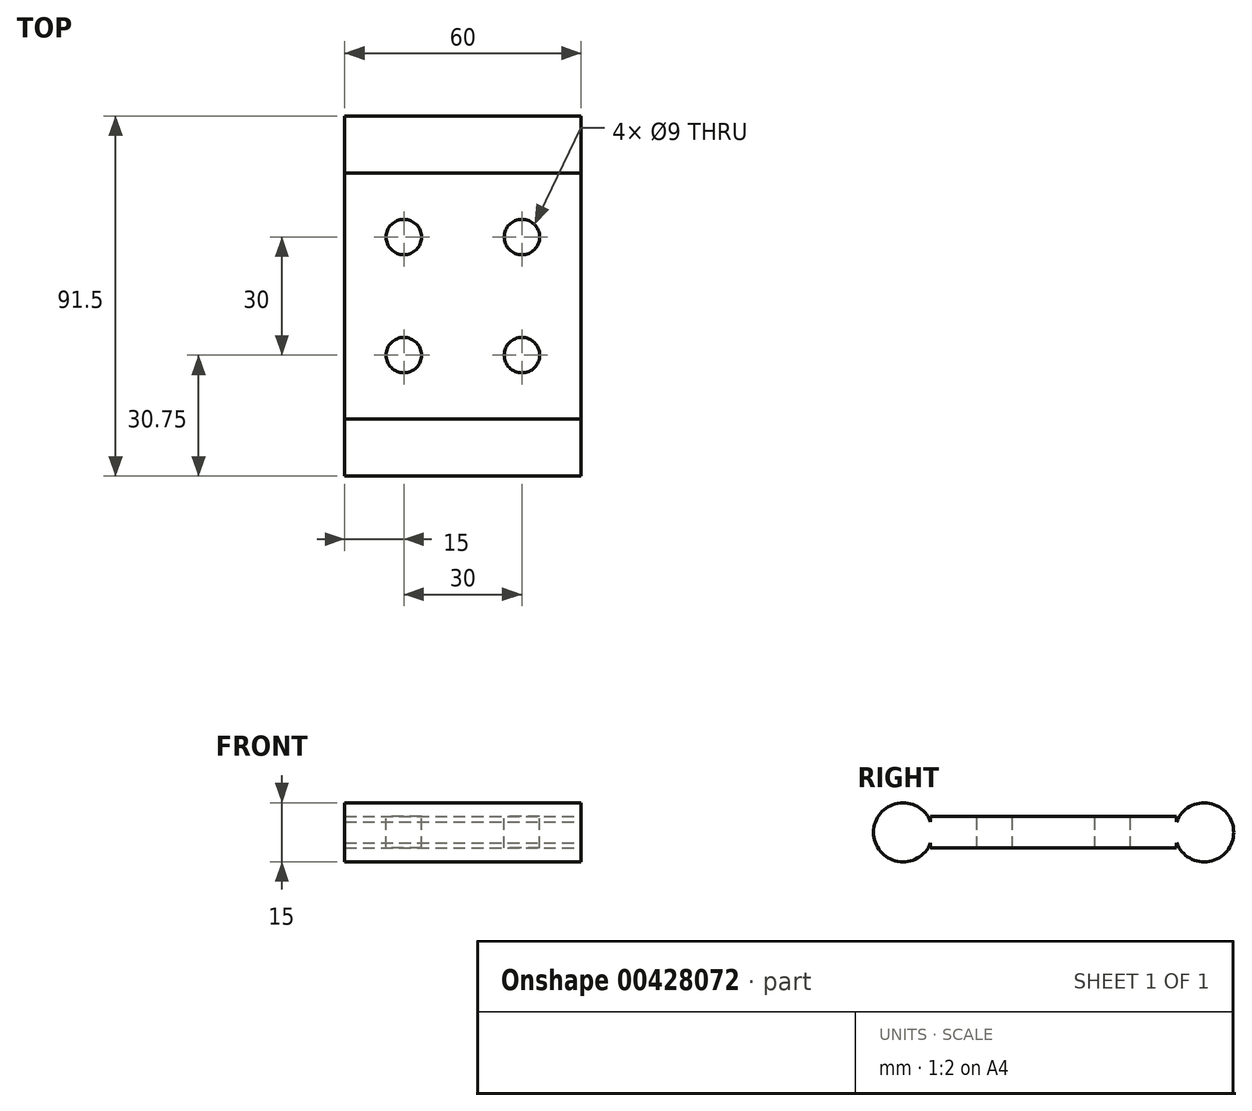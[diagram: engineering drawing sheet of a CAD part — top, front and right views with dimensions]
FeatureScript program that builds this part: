
annotation { "Feature Type Name" : "Feature", "Feature Type Description" : "" }
export const myFeature = defineFeature(function(context is Context, id is Id, definition is map)
    precondition{}
    {
        {
            var Q0;
            Q0=qCreatedBy(makeId("Top.planeOp"),FACE);
            var sketch = newSketch(context, id + "F0", { "sketchPlane" : qUnion([Q0])});
            skLineSegment(sketch, "E0.bottom", {"start": v(0, 0) * mm, "end": v(60, 0) * mm});
            skLineSegment(sketch, "E0.top", {"start": v(0, -62.5) * mm, "end": v(60, -62.5) * mm});
            skLineSegment(sketch, "E0.left", {"start": v(0, 0) * mm, "end": v(0, -62.5) * mm});
            skLineSegment(sketch, "E0.right", {"start": v(60, 0) * mm, "end": v(60, -62.5) * mm});
            skSolve(sketch);
        }
        {
            var Q0;
            Q0=makeQuery(id+"F0.imprint","IMPRINT",FACE,{"disambiguationData":[TD([[makeQuery(id+"F0.imprint","IMPRINT",EDGE,{"derivedFrom":sQuery(id+"F0.wireOp",EDGE,"E0.bottom")}),-1.0]])]});
            extrude(context, id + "F1", {"entities" : qUnion([Q0]), "depth" : 8 * mm});
        }
        {
            var Q0;
            Q0=makeQuery(id+"F1.opExtrude","CAP_FACE",FACE,{"disambiguationData":[OSD([sQuery(id+"F0.wireOp",EDGE,"E0.bottom"),sQuery(id+"F0.wireOp",EDGE,"E0.top"),sQuery(id+"F0.wireOp",EDGE,"E0.left"),sQuery(id+"F0.wireOp",EDGE,"E0.right")])],"isStart":false});
            var sketch = newSketch(context, id + "F2", { "sketchPlane" : qUnion([Q0])});
            skLineSegment(sketch, "E1", {"start": v(30, -16.25) * mm, "end": v(15, -16.25) * mm, "construction": true});
            skLineSegment(sketch, "E2", {"start": v(30, -16.25) * mm, "end": v(45, -16.25) * mm, "construction": true});
            skLineSegment(sketch, "E3", {"start": v(0, -31.25) * mm, "end": v(60, -31.25) * mm, "construction": true});
            skLineSegment(sketch, "E4.MirrorCS", {"start": v(30, -46.25) * mm, "end": v(45, -46.25) * mm, "construction": true});
            skLineSegment(sketch, "E5.MirrorCS", {"start": v(30, -46.25) * mm, "end": v(15, -46.25) * mm, "construction": true});
            skLineSegment(sketch, "E6", {"start": v(30, -31.25) * mm, "end": v(30, -16.25) * mm});
            skSolve(sketch);
        }
        {
            var Q0;
            Q0=sQuery(id+"F2.wireOp",VERTEX,"E1.end");
            var Q1;
            Q1=sQuery(id+"F2.wireOp",VERTEX,"E2.end");
            var Q2;
            Q2=sQuery(id+"F2.wireOp",VERTEX,"E4.MirrorCS.end");
            var Q3;
            Q3=sQuery(id+"F2.wireOp",VERTEX,"E5.MirrorCS.end");
            var Q4;
            Q4=makeQuery(id+"F1.opExtrude","SWEPT_BODY",BODY,{"disambiguationData":[OSD([sQuery(id+"F0.wireOp",EDGE,"E0.bottom"),sQuery(id+"F0.wireOp",EDGE,"E0.top"),sQuery(id+"F0.wireOp",EDGE,"E0.left"),sQuery(id+"F0.wireOp",EDGE,"E0.right")])]});
            hole(context, id + "F3", {"style" : HoleStyle.SIMPLE, "endStyle" : HoleEndStyle.BLIND, "holeDiameter" : 9 * mm, "holeDepth" : 15 * mm, "isTappedThrough" : true, "tappedDepth" : 12 * mm, "tapClearance" : 3, "locations" : qUnion([Q0, Q1, Q2, Q3]), "scope" : qUnion([Q4])});
        }
        {
            var Q0;
            Q0=makeQuery(id+"F1.opExtrude","SWEPT_FACE",FACE,{"disambiguationData":[OSD([sQuery(id+"F0.wireOp",EDGE,"E0.right")])]});
            var sketch = newSketch(context, id + "F4", { "sketchPlane" : qUnion([Q0])});
            skLineSegment(sketch, "E7", {"start": v(-62.5, 4) * mm, "end": v(-69.5, 4) * mm, "construction": true});
            skLineSegment(sketch, "E8", {"start": v(0, 4) * mm, "end": v(7, 4) * mm, "construction": true});
            skCircle(sketch, "E9", {"center": v(-69.5, 4) * mm, "radius": 7.5 * mm});
            skCircle(sketch, "E10", {"center": v(7, 4) * mm, "radius": 7.5 * mm});
            skSolve(sketch);
        }
        {
            var Q0;
            {var subQ0=sQuery(id+"F4.wireOp",EDGE,"E9");var subQ1=makeQuery(id+"F1.opExtrude","SWEPT_EDGE",EDGE,{"disambiguationData":[OSD([sQuery(id+"F0.wireOp",EDGE,"E0.top"),sQuery(id+"F0.wireOp",EDGE,"E0.right")])]});var subQ2=makeQuery(id+"F4.imprint","INTERSECT",VERTEX,{"disambiguationData":[OD(0.0)],"derivedFrom":[subQ1,subQ0]});Q0=makeQuery(id+"F4.imprint","IMPRINT",FACE,{"disambiguationData":[TD([[makeQuery(id+"F4.imprint","IMPRINT",EDGE,{"disambiguationData":[TD([[subQ2,1.0]])],"derivedFrom":subQ0}),1.0]])]});}
            var Q1;
            {var subQ0=sQuery(id+"F4.wireOp",EDGE,"E10");var subQ1=makeQuery(id+"F1.opExtrude","SWEPT_EDGE",EDGE,{"disambiguationData":[OSD([sQuery(id+"F0.wireOp",EDGE,"E0.bottom"),sQuery(id+"F0.wireOp",EDGE,"E0.right")])]});var subQ2=makeQuery(id+"F4.imprint","INTERSECT",VERTEX,{"disambiguationData":[OD(0.0)],"derivedFrom":[subQ1,subQ0]});Q1=makeQuery(id+"F4.imprint","IMPRINT",FACE,{"disambiguationData":[TD([[makeQuery(id+"F4.imprint","IMPRINT",EDGE,{"disambiguationData":[TD([[subQ2,-1.0]])],"derivedFrom":subQ0}),1.0]])]});}
            extrude(context, id + "F5", {"entities" : qUnion([Q0, Q1]), "operationType" : NewBodyOperationType.ADD, "oppositeDirection" : true, "depth" : 60 * mm});
        }
    });
